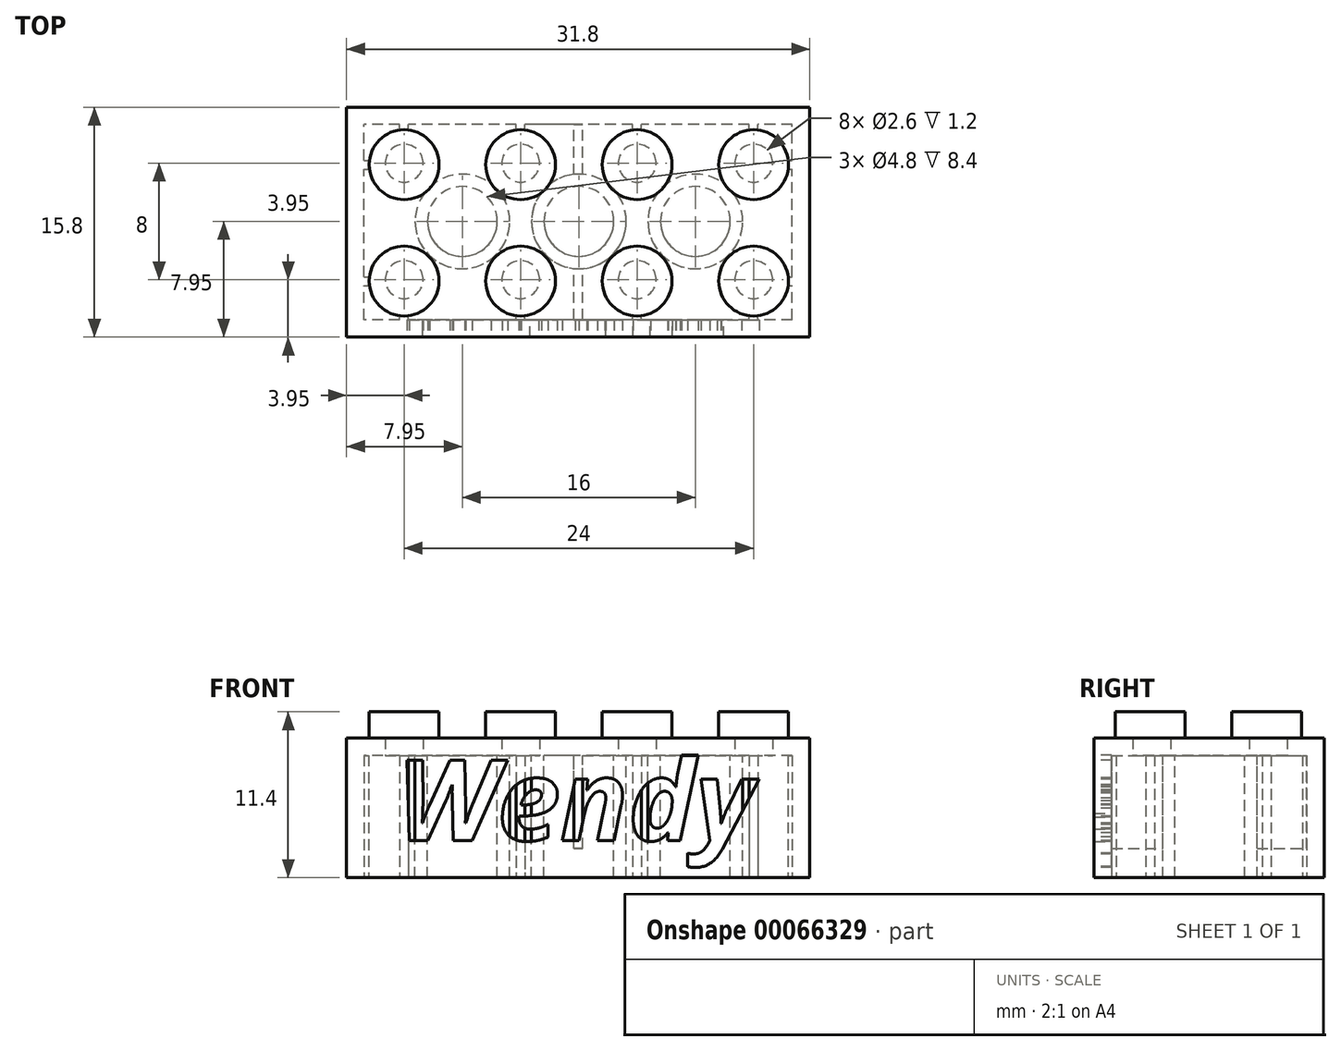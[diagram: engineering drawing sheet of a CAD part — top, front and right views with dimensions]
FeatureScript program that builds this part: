
annotation { "Feature Type Name" : "Feature", "Feature Type Description" : "" }
export const myFeature = defineFeature(function(context is Context, id is Id, definition is map)
    precondition{}
    {
        {
            var Q0;
            Q0=qCreatedBy(makeId("Top.planeOp"),FACE);
            var sketch = newSketch(context, id + "F0", { "sketchPlane" : qUnion([Q0])});
            skLineSegment(sketch, "E0.rect.bottom", {"start": v(15.9, -7.9) * mm, "end": v(-15.9, -7.9) * mm});
            skLineSegment(sketch, "E0.rect.top", {"start": v(15.9, 7.9) * mm, "end": v(-15.9, 7.9) * mm});
            skLineSegment(sketch, "E0.rect.left", {"start": v(15.9, -7.9) * mm, "end": v(15.9, 7.9) * mm});
            skLineSegment(sketch, "E0.rect.right", {"start": v(-15.9, -7.9) * mm, "end": v(-15.9, 7.9) * mm});
            skPoint(sketch, "E0.rect.middle", {"position": v(0, 0) * mm});
            skSolve(sketch);
        }
        {
            var Q0;
            Q0 = qSketchRegion(id + "F0", true);
            extrude(context, id + "F1", {"entities" : qUnion([Q0]), "depth" : 9.6 * mm});
        }
        {
            var Q0;
            Q0=makeQuery(id+"F1.opExtrude","CAP_FACE",FACE,{"disambiguationData":[OSD([sQuery(id+"F0.wireOp",EDGE,"E0.rect.bottom"),sQuery(id+"F0.wireOp",EDGE,"E0.rect.top"),sQuery(id+"F0.wireOp",EDGE,"E0.rect.left"),sQuery(id+"F0.wireOp",EDGE,"E0.rect.right")])],"isStart":true});
            var sketch = newSketch(context, id + "F2", { "sketchPlane" : qUnion([Q0])});
            skLineSegment(sketch, "E1.rect.bottom", {"start": v(14.7, 6.7) * mm, "end": v(-14.7, 6.7) * mm});
            skLineSegment(sketch, "E1.rect.top", {"start": v(14.7, -6.7) * mm, "end": v(-14.7, -6.7) * mm});
            skLineSegment(sketch, "E1.rect.left", {"start": v(14.7, 6.7) * mm, "end": v(14.7, -6.7) * mm});
            skLineSegment(sketch, "E1.rect.right", {"start": v(-14.7, 6.7) * mm, "end": v(-14.7, -6.7) * mm});
            skPoint(sketch, "E1.rect.middle", {"position": v(0, 0) * mm});
            skSolve(sketch);
        }
        {
            var Q0;
            Q0 = qSketchRegion(id + "F2", true);
            extrude(context, id + "F3", {"entities" : qUnion([Q0]), "operationType" : NewBodyOperationType.REMOVE, "oppositeDirection" : true, "depth" : 8.4 * mm});
        }
        {
            var Q0;
            Q0=makeQuery(id+"F1.opExtrude","CAP_FACE",FACE,{"disambiguationData":[OSD([sQuery(id+"F0.wireOp",EDGE,"E0.rect.bottom"),sQuery(id+"F0.wireOp",EDGE,"E0.rect.top"),sQuery(id+"F0.wireOp",EDGE,"E0.rect.left"),sQuery(id+"F0.wireOp",EDGE,"E0.rect.right")])],"isStart":false});
            var sketch = newSketch(context, id + "F4", { "sketchPlane" : qUnion([Q0])});
            skLineSegment(sketch, "E2", {"start": v(-14.8, 0) * mm, "end": v(12.63, 0) * mm});
            skCircle(sketch, "E3", {"center": v(-11.95, 3.95) * mm, "radius": 2.4 * mm});
            skCircle(sketch, "E4.0.1.0", {"center": v(-11.95, -4.05) * mm, "radius": 2.4 * mm});
            skCircle(sketch, "E4.1.0.0", {"center": v(-3.95, 3.95) * mm, "radius": 2.4 * mm});
            skCircle(sketch, "E4.1.1.0", {"center": v(-3.95, -4.05) * mm, "radius": 2.4 * mm});
            skCircle(sketch, "E4.2.0.0", {"center": v(4.05, 3.95) * mm, "radius": 2.4 * mm});
            skCircle(sketch, "E4.2.1.0", {"center": v(4.05, -4.05) * mm, "radius": 2.4 * mm});
            skCircle(sketch, "E4.3.0.0", {"center": v(12.05, 3.95) * mm, "radius": 2.4 * mm});
            skCircle(sketch, "E4.3.1.0", {"center": v(12.05, -4.05) * mm, "radius": 2.4 * mm});
            skLineSegment(sketch, "E4.direction1", {"start": v(-11.95, 3.95) * mm, "end": v(-3.95, 3.95) * mm, "construction": true});
            skLineSegment(sketch, "E4.direction2", {"start": v(-11.95, 3.95) * mm, "end": v(-11.95, -4.05) * mm, "construction": true});
            skSolve(sketch);
        }
        {
            var Q0;
            Q0 = qSketchRegion(id + "F4", true);
            extrude(context, id + "F5", {"entities" : qUnion([Q0]), "operationType" : NewBodyOperationType.ADD, "depth" : 1.8 * mm});
        }
        {
            var Q0;
            Q0=makeQuery(id+"F3.boolean.opBoolean","COPY",FACE,{"derivedFrom":makeQuery(id+"F3.opExtrude","CAP_FACE",FACE,{"disambiguationData":[OSD([sQuery(id+"F2.wireOp",EDGE,"E1.rect.bottom"),sQuery(id+"F2.wireOp",EDGE,"E1.rect.top"),sQuery(id+"F2.wireOp",EDGE,"E1.rect.left"),sQuery(id+"F2.wireOp",EDGE,"E1.rect.right")])],"isStart":false})});
            var sketch = newSketch(context, id + "F6", { "sketchPlane" : qUnion([Q0])});
            skCircle(sketch, "E5", {"center": v(-11.95, 3.95) * mm, "radius": 1.3 * mm});
            skCircle(sketch, "E6.0.1.0", {"center": v(-11.95, -4.05) * mm, "radius": 1.3 * mm});
            skCircle(sketch, "E6.1.0.0", {"center": v(-3.95, 3.95) * mm, "radius": 1.3 * mm});
            skCircle(sketch, "E6.1.1.0", {"center": v(-3.95, -4.05) * mm, "radius": 1.3 * mm});
            skCircle(sketch, "E6.2.0.0", {"center": v(4.05, 3.95) * mm, "radius": 1.3 * mm});
            skCircle(sketch, "E6.2.1.0", {"center": v(4.05, -4.05) * mm, "radius": 1.3 * mm});
            skCircle(sketch, "E6.3.0.0", {"center": v(12.05, 3.95) * mm, "radius": 1.3 * mm});
            skCircle(sketch, "E6.3.1.0", {"center": v(12.05, -4.05) * mm, "radius": 1.3 * mm});
            skLineSegment(sketch, "E6.direction1", {"start": v(-11.95, 3.95) * mm, "end": v(-3.95, 3.95) * mm, "construction": true});
            skLineSegment(sketch, "E6.direction2", {"start": v(-11.95, 3.95) * mm, "end": v(-11.95, -4.05) * mm, "construction": true});
            skSolve(sketch);
        }
        {
            var Q0;
            Q0 = qSketchRegion(id + "F6", true);
            extrude(context, id + "F7", {"entities" : qUnion([Q0]), "operationType" : NewBodyOperationType.REMOVE, "oppositeDirection" : true, "depth" : 1.2 * mm});
        }
        {
            var Q0;
            Q0=makeQuery(id+"F3.boolean.opBoolean","COPY",FACE,{"derivedFrom":makeQuery(id+"F3.opExtrude","CAP_FACE",FACE,{"disambiguationData":[OSD([sQuery(id+"F2.wireOp",EDGE,"E1.rect.bottom"),sQuery(id+"F2.wireOp",EDGE,"E1.rect.top"),sQuery(id+"F2.wireOp",EDGE,"E1.rect.left"),sQuery(id+"F2.wireOp",EDGE,"E1.rect.right")])],"isStart":false})});
            var sketch = newSketch(context, id + "F8", { "sketchPlane" : qUnion([Q0])});
            skLineSegment(sketch, "E7", {"start": v(-11.95, 3.95) * mm, "end": v(-3.95, -4.05) * mm, "construction": true});
            skLineSegment(sketch, "E8", {"start": v(-11.95, -4.05) * mm, "end": v(-3.95, 3.95) * mm, "construction": true});
            skLineSegment(sketch, "E9", {"start": v(4.05, 3.95) * mm, "end": v(12.05, -4.05) * mm, "construction": true});
            skLineSegment(sketch, "E10", {"start": v(4.05, -4.05) * mm, "end": v(12.05, 3.95) * mm, "construction": true});
            skLineSegment(sketch, "E11", {"start": v(-3.95, 3.95) * mm, "end": v(4.05, -4.05) * mm, "construction": true});
            skLineSegment(sketch, "E12", {"start": v(-3.95, -4.05) * mm, "end": v(4.05, 3.95) * mm, "construction": true});
            skCircle(sketch, "E13", {"center": v(-7.95, -0.05) * mm, "radius": 2.4 * mm});
            skCircle(sketch, "E14", {"center": v(-7.95, -0.05) * mm, "radius": 3.25 * mm});
            skCircle(sketch, "E15.1.0.0", {"center": v(0.05, -0.05) * mm, "radius": 2.4 * mm});
            skCircle(sketch, "E15.2.0.0", {"center": v(8.05, -0.05) * mm, "radius": 2.4 * mm});
            skLineSegment(sketch, "E15.direction1", {"start": v(-7.95, -0.05) * mm, "end": v(0.05, -0.05) * mm, "construction": true});
            skCircle(sketch, "E16.1.0.0", {"center": v(0.05, -0.05) * mm, "radius": 3.25 * mm});
            skCircle(sketch, "E16.2.0.0", {"center": v(8.05, -0.05) * mm, "radius": 3.25 * mm});
            skSolve(sketch);
        }
        {
            var Q0;
            Q0 = qSketchRegion(id + "F8", true);
            var Q1;
            Q1=makeQuery(id+"F1.opExtrude","CAP_FACE",FACE,{"disambiguationData":[OSD([sQuery(id+"F0.wireOp",EDGE,"E0.rect.bottom"),sQuery(id+"F0.wireOp",EDGE,"E0.rect.top"),sQuery(id+"F0.wireOp",EDGE,"E0.rect.left"),sQuery(id+"F0.wireOp",EDGE,"E0.rect.right")])],"isStart":true});
            extrude(context, id + "F9", {"entities" : qUnion([Q0]), "operationType" : NewBodyOperationType.ADD, "endBound" : BoundingType.UP_TO_SURFACE, "endBoundEntityFace" : qUnion([Q1]), "depth" : 25 * mm});
        }
        {
            var Q0;
            Q0=makeQuery(id+"F1.opExtrude","CAP_FACE",FACE,{"disambiguationData":[OSD([sQuery(id+"F0.wireOp",EDGE,"E0.rect.bottom"),sQuery(id+"F0.wireOp",EDGE,"E0.rect.top"),sQuery(id+"F0.wireOp",EDGE,"E0.rect.left"),sQuery(id+"F0.wireOp",EDGE,"E0.rect.right")])],"isStart":true});
            var sketch = newSketch(context, id + "F10", { "sketchPlane" : qUnion([Q0])});
            skLineSegment(sketch, "E17.bottom", {"start": v(-12.25, 6.7) * mm, "end": v(-11.65, 6.7) * mm});
            skLineSegment(sketch, "E17.top", {"start": v(-12.25, 6.4) * mm, "end": v(-11.65, 6.4) * mm});
            skLineSegment(sketch, "E17.left", {"start": v(-12.25, 6.7) * mm, "end": v(-12.25, 6.4) * mm});
            skLineSegment(sketch, "E17.right", {"start": v(-11.65, 6.7) * mm, "end": v(-11.65, 6.4) * mm});
            skLineSegment(sketch, "E18", {"start": v(-11.95, 15.14) * mm, "end": v(-11.95, -3.95) * mm, "construction": true});
            skLineSegment(sketch, "E19.0.1.0", {"start": v(-12.25, -6.7) * mm, "end": v(-11.65, -6.7) * mm});
            skLineSegment(sketch, "E19.0.1.1", {"start": v(-11.65, -6.4) * mm, "end": v(-11.65, -6.7) * mm});
            skLineSegment(sketch, "E19.0.1.2", {"start": v(-12.25, -6.4) * mm, "end": v(-11.65, -6.4) * mm});
            skLineSegment(sketch, "E19.0.1.3", {"start": v(-12.25, -6.4) * mm, "end": v(-12.25, -6.7) * mm});
            skLineSegment(sketch, "E19.1.0.0", {"start": v(-4.25, 6.4) * mm, "end": v(-3.65, 6.4) * mm});
            skLineSegment(sketch, "E19.1.0.1", {"start": v(-3.65, 6.7) * mm, "end": v(-3.65, 6.4) * mm});
            skLineSegment(sketch, "E19.1.0.2", {"start": v(-4.25, 6.7) * mm, "end": v(-3.65, 6.7) * mm});
            skLineSegment(sketch, "E19.1.0.3", {"start": v(-4.25, 6.7) * mm, "end": v(-4.25, 6.4) * mm});
            skLineSegment(sketch, "E19.1.1.0", {"start": v(-4.25, -6.7) * mm, "end": v(-3.65, -6.7) * mm});
            skLineSegment(sketch, "E19.1.1.1", {"start": v(-3.65, -6.4) * mm, "end": v(-3.65, -6.7) * mm});
            skLineSegment(sketch, "E19.1.1.2", {"start": v(-4.25, -6.4) * mm, "end": v(-3.65, -6.4) * mm});
            skLineSegment(sketch, "E19.1.1.3", {"start": v(-4.25, -6.4) * mm, "end": v(-4.25, -6.7) * mm});
            skLineSegment(sketch, "E19.2.0.0", {"start": v(3.75, 6.4) * mm, "end": v(4.35, 6.4) * mm});
            skLineSegment(sketch, "E19.2.0.1", {"start": v(4.35, 6.7) * mm, "end": v(4.35, 6.4) * mm});
            skLineSegment(sketch, "E19.2.0.2", {"start": v(3.75, 6.7) * mm, "end": v(4.35, 6.7) * mm});
            skLineSegment(sketch, "E19.2.0.3", {"start": v(3.75, 6.7) * mm, "end": v(3.75, 6.4) * mm});
            skLineSegment(sketch, "E19.2.1.0", {"start": v(3.75, -6.7) * mm, "end": v(4.35, -6.7) * mm});
            skLineSegment(sketch, "E19.2.1.1", {"start": v(4.35, -6.4) * mm, "end": v(4.35, -6.7) * mm});
            skLineSegment(sketch, "E19.2.1.2", {"start": v(3.75, -6.4) * mm, "end": v(4.35, -6.4) * mm});
            skLineSegment(sketch, "E19.2.1.3", {"start": v(3.75, -6.4) * mm, "end": v(3.75, -6.7) * mm});
            skLineSegment(sketch, "E19.3.0.0", {"start": v(11.75, 6.4) * mm, "end": v(12.35, 6.4) * mm});
            skLineSegment(sketch, "E19.3.0.1", {"start": v(12.35, 6.7) * mm, "end": v(12.35, 6.4) * mm});
            skLineSegment(sketch, "E19.3.0.2", {"start": v(11.75, 6.7) * mm, "end": v(12.35, 6.7) * mm});
            skLineSegment(sketch, "E19.3.0.3", {"start": v(11.75, 6.7) * mm, "end": v(11.75, 6.4) * mm});
            skLineSegment(sketch, "E19.3.1.0", {"start": v(11.75, -6.7) * mm, "end": v(12.35, -6.7) * mm});
            skLineSegment(sketch, "E19.3.1.1", {"start": v(12.35, -6.4) * mm, "end": v(12.35, -6.7) * mm});
            skLineSegment(sketch, "E19.3.1.2", {"start": v(11.75, -6.4) * mm, "end": v(12.35, -6.4) * mm});
            skLineSegment(sketch, "E19.3.1.3", {"start": v(11.75, -6.4) * mm, "end": v(11.75, -6.7) * mm});
            skLineSegment(sketch, "E19.direction1", {"start": v(-12.25, 6.4) * mm, "end": v(-4.25, 6.4) * mm, "construction": true});
            skLineSegment(sketch, "E19.direction2", {"start": v(-12.25, 6.4) * mm, "end": v(-12.25, -6.7) * mm, "construction": true});
            skSolve(sketch);
        }
        {
            var Q0;
            Q0 = qSketchRegion(id + "F10", true);
            extrude(context, id + "F11", {"entities" : qUnion([Q0]), "operationType" : NewBodyOperationType.ADD, "oppositeDirection" : true, "depth" : 8.6 * mm});
        }
        {
            var Q0;
            Q0=qCreatedBy(makeId("Top.planeOp"),FACE);
            var sketch = newSketch(context, id + "F12", { "sketchPlane" : qUnion([Q0])});
            skLineSegment(sketch, "E20", {"start": v(-27.34, -4.05) * mm, "end": v(-11.95, -4.05) * mm, "construction": true});
            skLineSegment(sketch, "E21.bottom", {"start": v(-14.7, -4.35) * mm, "end": v(-14.4, -4.35) * mm});
            skLineSegment(sketch, "E21.top", {"start": v(-14.7, -3.75) * mm, "end": v(-14.4, -3.75) * mm});
            skLineSegment(sketch, "E21.left", {"start": v(-14.7, -4.35) * mm, "end": v(-14.7, -3.75) * mm});
            skLineSegment(sketch, "E21.right", {"start": v(-14.4, -4.35) * mm, "end": v(-14.4, -3.75) * mm});
            skLineSegment(sketch, "E22.0.1.0", {"start": v(-14.7, 3.65) * mm, "end": v(-14.4, 3.65) * mm});
            skLineSegment(sketch, "E22.0.1.1", {"start": v(-14.7, 3.65) * mm, "end": v(-14.7, 4.25) * mm});
            skLineSegment(sketch, "E22.0.1.2", {"start": v(-14.7, 4.25) * mm, "end": v(-14.4, 4.25) * mm});
            skLineSegment(sketch, "E22.0.1.3", {"start": v(-14.4, 3.65) * mm, "end": v(-14.4, 4.25) * mm});
            skLineSegment(sketch, "E22.1.0.0", {"start": v(14.4, -4.35) * mm, "end": v(14.7, -4.35) * mm});
            skLineSegment(sketch, "E22.1.0.1", {"start": v(14.4, -4.35) * mm, "end": v(14.4, -3.75) * mm});
            skLineSegment(sketch, "E22.1.0.2", {"start": v(14.4, -3.75) * mm, "end": v(14.7, -3.75) * mm});
            skLineSegment(sketch, "E22.1.0.3", {"start": v(14.7, -4.35) * mm, "end": v(14.7, -3.75) * mm});
            skLineSegment(sketch, "E22.1.1.0", {"start": v(14.4, 3.65) * mm, "end": v(14.7, 3.65) * mm});
            skLineSegment(sketch, "E22.1.1.1", {"start": v(14.4, 3.65) * mm, "end": v(14.4, 4.25) * mm});
            skLineSegment(sketch, "E22.1.1.2", {"start": v(14.4, 4.25) * mm, "end": v(14.7, 4.25) * mm});
            skLineSegment(sketch, "E22.1.1.3", {"start": v(14.7, 3.65) * mm, "end": v(14.7, 4.25) * mm});
            skLineSegment(sketch, "E22.direction1", {"start": v(-14.7, -4.35) * mm, "end": v(14.4, -4.35) * mm, "construction": true});
            skLineSegment(sketch, "E22.direction2", {"start": v(-14.7, -4.35) * mm, "end": v(-14.7, 3.65) * mm, "construction": true});
            skSolve(sketch);
        }
        {
            var Q0;
            Q0 = qSketchRegion(id + "F12", true);
            extrude(context, id + "F13", {"entities" : qUnion([Q0]), "operationType" : NewBodyOperationType.ADD, "depth" : 8.6 * mm});
        }
        {
            var Q0;
            {var subQ0=sQuery(id+"F2.wireOp",EDGE,"E1.rect.bottom");var subQ1=sQuery(id+"F2.wireOp",EDGE,"E1.rect.top");var subQ2=sQuery(id+"F2.wireOp",EDGE,"E1.rect.left");var subQ3=sQuery(id+"F2.wireOp",EDGE,"E1.rect.right");Q0=makeQuery(id+"F9.boolean.opBoolean","SPLIT",FACE,{"disambiguationData":[TD([makeQuery(id+"F3.boolean.opBoolean","COPY",FACE,{"derivedFrom":makeQuery(id+"F3.opExtrude","SWEPT_FACE",FACE,{"disambiguationData":[OSD([subQ0])]})})])],"derivedFrom":makeQuery(id+"F3.boolean.opBoolean","COPY",FACE,{"derivedFrom":makeQuery(id+"F3.opExtrude","CAP_FACE",FACE,{"disambiguationData":[OSD([subQ0,subQ1,subQ2,subQ3])],"isStart":false})})});}
            var sketch = newSketch(context, id + "F14", { "sketchPlane" : qUnion([Q0])});
            skLineSegment(sketch, "E23.bottom", {"start": v(-0.3, 7) * mm, "end": v(0.3, 7) * mm});
            skLineSegment(sketch, "E23.top", {"start": v(-0.3, 3) * mm, "end": v(0.3, 3) * mm});
            skLineSegment(sketch, "E23.left", {"start": v(-0.3, 7) * mm, "end": v(-0.3, 3) * mm});
            skLineSegment(sketch, "E23.right", {"start": v(0.3, 7) * mm, "end": v(0.3, 3) * mm});
            skSolve(sketch);
        }
        {
            var Q0;
            Q0 = qSketchRegion(id + "F14", true);
            extrude(context, id + "F15", {"entities" : qUnion([Q0]), "operationType" : NewBodyOperationType.ADD, "depth" : 6.4 * mm});
        }
        {
            var Q0;
            {var subQ0=sQuery(id+"F2.wireOp",EDGE,"E1.rect.bottom");var subQ1=sQuery(id+"F2.wireOp",EDGE,"E1.rect.top");var subQ2=sQuery(id+"F2.wireOp",EDGE,"E1.rect.left");var subQ3=sQuery(id+"F2.wireOp",EDGE,"E1.rect.right");Q0=makeQuery(id+"F9.boolean.opBoolean","SPLIT",FACE,{"disambiguationData":[TD([makeQuery(id+"F3.boolean.opBoolean","COPY",FACE,{"derivedFrom":makeQuery(id+"F3.opExtrude","SWEPT_FACE",FACE,{"disambiguationData":[OSD([subQ0])]})})])],"derivedFrom":makeQuery(id+"F3.boolean.opBoolean","COPY",FACE,{"derivedFrom":makeQuery(id+"F3.opExtrude","CAP_FACE",FACE,{"disambiguationData":[OSD([subQ0,subQ1,subQ2,subQ3])],"isStart":false})})});}
            var sketch = newSketch(context, id + "F16", { "sketchPlane" : qUnion([Q0])});
            skLineSegment(sketch, "E24.bottom", {"start": v(-0.3, -3.05) * mm, "end": v(0.3, -3.05) * mm});
            skLineSegment(sketch, "E24.top", {"start": v(-0.3, -7.05) * mm, "end": v(0.3, -7.05) * mm});
            skLineSegment(sketch, "E24.left", {"start": v(-0.3, -3.05) * mm, "end": v(-0.3, -7.05) * mm});
            skLineSegment(sketch, "E24.right", {"start": v(0.3, -3.05) * mm, "end": v(0.3, -7.05) * mm});
            skSolve(sketch);
        }
        {
            var Q0;
            Q0 = qSketchRegion(id + "F16", true);
            extrude(context, id + "F17", {"entities" : qUnion([Q0]), "operationType" : NewBodyOperationType.ADD, "depth" : 6.4 * mm});
        }
        {
            var Q0;
            Q0=makeQuery(id+"F1.opExtrude","SWEPT_FACE",FACE,{"disambiguationData":[OSD([sQuery(id+"F0.wireOp",EDGE,"E0.rect.bottom")])]});
            var sketch = newSketch(context, id + "F18", { "sketchPlane" : qUnion([Q0])});
            skText(sketch, "E25", { "text": "Wendy", "fontName": "OpenSans-BoldItalic.ttf"});
            const initialGuessF18  = {"E25": [-0.01246, 0.00256, 1, 0, 0.00557]};
            skSetInitialGuess(sketch, initialGuessF18);
            skSolve(sketch);
        }
        {
            var Q0;
            Q0 = qSketchRegion(id + "F18", true);
            extrude(context, id + "F19", {"entities" : qUnion([Q0]), "operationType" : NewBodyOperationType.REMOVE, "oppositeDirection" : true, "depth" : 1.2 * mm});
        }
    });
